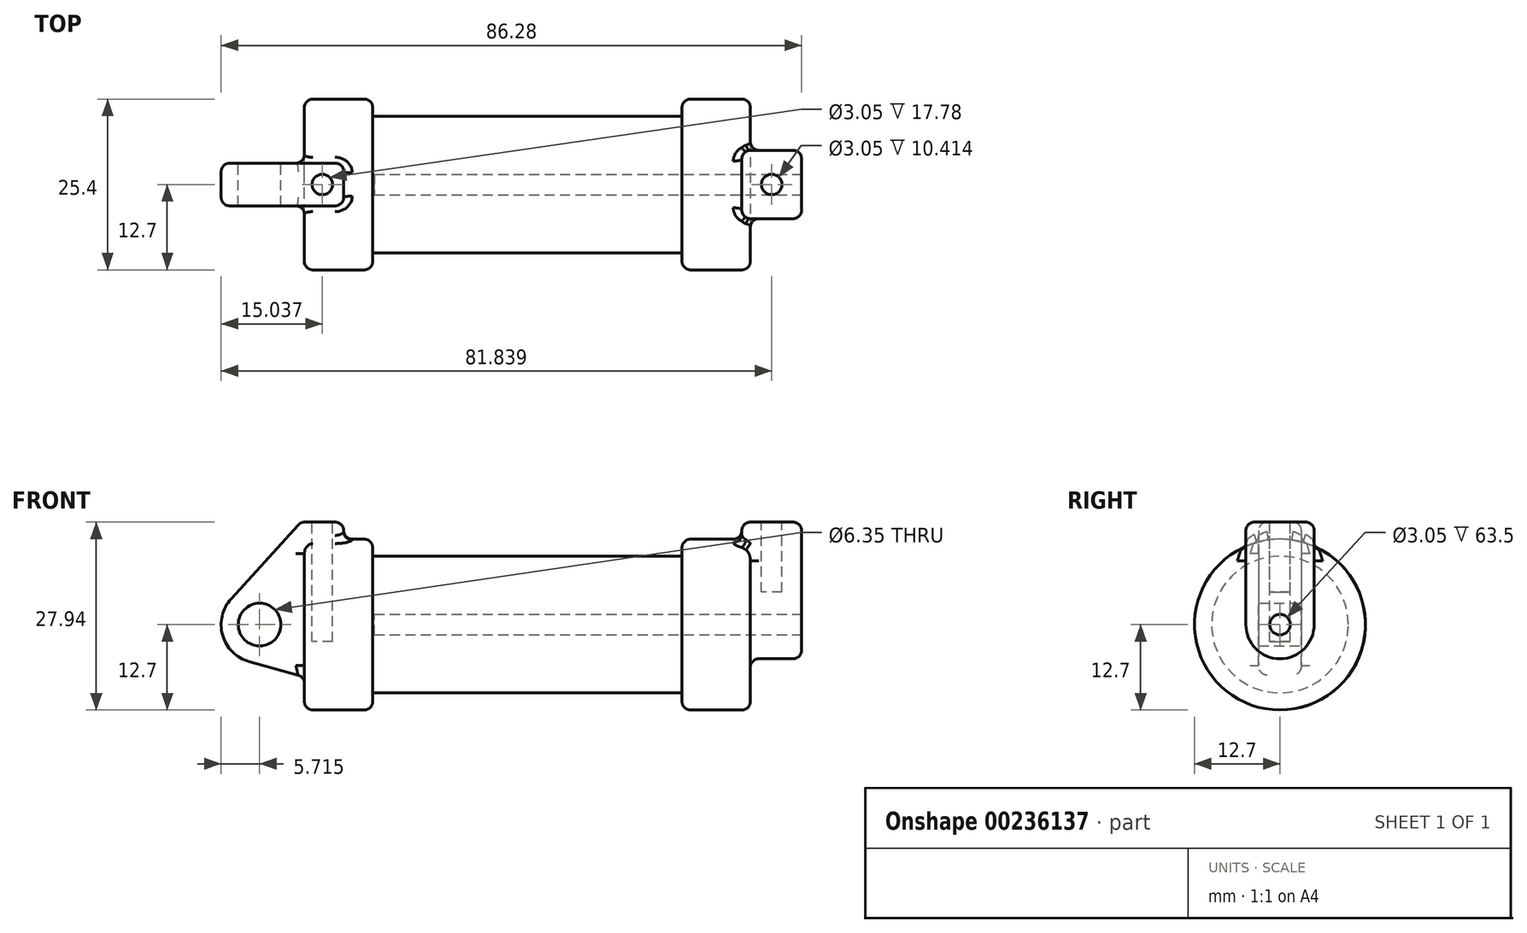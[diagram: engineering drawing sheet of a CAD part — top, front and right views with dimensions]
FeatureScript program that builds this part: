
annotation { "Feature Type Name" : "Feature", "Feature Type Description" : "" }
export const myFeature = defineFeature(function(context is Context, id is Id, definition is map)
    precondition{}
    {
        {
            var Q0;
            Q0=qCreatedBy(makeId("Front.planeOp"),FACE);
            var sketch = newSketch(context, id + "F0", { "sketchPlane" : qUnion([Q0])});
            skLineSegment(sketch, "E0", {"start": v(0, 0) * mm, "end": v(0, 12.7) * mm});
            skLineSegment(sketch, "E1", {"start": v(0, 12.7) * mm, "end": v(10.16, 12.7) * mm});
            skLineSegment(sketch, "E2", {"start": v(10.16, 12.7) * mm, "end": v(10.16, 10.16) * mm});
            skLineSegment(sketch, "E3", {"start": v(10.16, 10.16) * mm, "end": v(56.13, 10.16) * mm});
            skLineSegment(sketch, "E4", {"start": v(56.13, 10.16) * mm, "end": v(56.13, 12.7) * mm});
            skLineSegment(sketch, "E5", {"start": v(56.13, 12.7) * mm, "end": v(66.3, 12.7) * mm});
            skLineSegment(sketch, "E6", {"start": v(66.3, 12.7) * mm, "end": v(66.3, 0) * mm});
            skLineSegment(sketch, "E7", {"start": v(66.3, 0) * mm, "end": v(0, 0) * mm});
            skLineSegment(sketch, "E8", {"start": v(5.84, 15.24) * mm, "end": v(-0.5, 15.24) * mm});
            skLineSegment(sketch, "E9", {"start": v(-0.5, 15.24) * mm, "end": v(-10.88, 3.85) * mm});
            skLineSegment(sketch, "E10", {"start": v(0, 0) * mm, "end": v(-6.65, 0) * mm});
            skCircle(sketch, "E11", {"center": v(-6.65, 0) * mm, "radius": 5.72 * mm});
            skCircle(sketch, "E12", {"center": v(-6.65, 0) * mm, "radius": 3.18 * mm});
            skLineSegment(sketch, "E13", {"start": v(5.84, 15.24) * mm, "end": v(5.84, -9.4) * mm});
            skLineSegment(sketch, "E14", {"start": v(5.84, -9.4) * mm, "end": v(-8.18, -5.5) * mm});
            skSolve(sketch);
        }
        {
            var Q0;
            {var subQ0=sQuery(id+"F0.wireOp",EDGE,"E2");Q0=makeQuery(id+"F0.imprint","IMPRINT",FACE,{"disambiguationData":[TD([[makeQuery(id+"F0.imprint","IMPRINT",EDGE,{"derivedFrom":subQ0}),-1.0]])]});}
            var Q1;
            {var subQ0=sQuery(id+"F0.wireOp",EDGE,"E0");Q1=makeQuery(id+"F0.imprint","IMPRINT",FACE,{"disambiguationData":[TD([[makeQuery(id+"F0.imprint","IMPRINT",EDGE,{"derivedFrom":subQ0}),-1.0]])]});}
            var Q2;
            Q2=sQuery(id+"F0.wireOp",EDGE,"E7");
            revolve(context, id + "F1", {"entities" : qUnion([Q0, Q1]), "axis" : qUnion([Q2]), "revolveType" : RevolveType.FULL});
        }
        {
            var Q0;
            {var subQ0=sQuery(id+"F0.wireOp",EDGE,"E0");Q0=makeQuery(id+"F0.imprint","IMPRINT",FACE,{"disambiguationData":[TD([[makeQuery(id+"F0.imprint","IMPRINT",EDGE,{"derivedFrom":subQ0}),-1.0]])]});}
            var Q1;
            {var subQ0=sQuery(id+"F0.wireOp",EDGE,"E14");Q1=makeQuery(id+"F0.imprint","IMPRINT",FACE,{"disambiguationData":[TD([[makeQuery(id+"F0.imprint","IMPRINT",EDGE,{"derivedFrom":subQ0}),-1.0]])]});}
            var Q2;
            {var subQ4=sQuery(id+"F0.wireOp",EDGE,"E12");Q2=makeQuery(id+"F0.imprint","IMPRINT",FACE,{"disambiguationData":[TD([[makeQuery(id+"F0.imprint","IMPRINT",EDGE,{"derivedFrom":subQ4}),-1.0]])]});}
            var Q3;
            {var subQ3=sQuery(id+"F0.wireOp",EDGE,"E0");Q3=makeQuery(id+"F0.imprint","IMPRINT",FACE,{"disambiguationData":[TD([[makeQuery(id+"F0.imprint","IMPRINT",EDGE,{"derivedFrom":subQ3}),1.0]])]});}
            extrude(context, id + "F2", {"entities" : qUnion([Q0, Q1, Q2, Q3]), "operationType" : NewBodyOperationType.ADD, "endBound" : BoundingType.SYMMETRIC, "depth" : 6.35 * mm});
        }
        {
            var Q0;
            Q0=makeQuery(id+"F1.opRevolve","SWEPT_FACE",FACE,{"disambiguationData":[OSD([sQuery(id+"F0.wireOp",EDGE,"E6")])]});
            var sketch = newSketch(context, id + "F3", { "sketchPlane" : qUnion([Q0])});
            skCircle(sketch, "E15", {"center": v(0, 0) * mm, "radius": 5.08 * mm});
            skLineSegment(sketch, "E16", {"start": v(5.08, 0) * mm, "end": v(5.08, 15.24) * mm});
            skLineSegment(sketch, "E17", {"start": v(5.08, 15.24) * mm, "end": v(-5.08, 15.24) * mm});
            skLineSegment(sketch, "E18", {"start": v(-5.08, 15.24) * mm, "end": v(-5.08, 0) * mm});
            skSolve(sketch);
        }
        {
            var Q0;
            Q0 = qSketchRegion(id + "F3", true);
            extrude(context, id + "F4", {"entities" : qUnion([Q0]), "operationType" : NewBodyOperationType.ADD, "depth" : 7.62 * mm, "hasSecondDirection" : true, "secondDirectionOppositeDirection" : true, "secondDirectionDepth" : 1.27 * mm});
        }
        {
            var Q0;
            Q0=makeQuery(id+"F4.opExtrude","CAP_FACE",FACE,{"disambiguationData":[OSD([sQuery(id+"F3.wireOp",EDGE,"E15"),sQuery(id+"F3.wireOp",EDGE,"E16"),sQuery(id+"F3.wireOp",EDGE,"E17"),sQuery(id+"F3.wireOp",EDGE,"E18")])],"isStart":false});
            var sketch = newSketch(context, id + "F5", { "sketchPlane" : qUnion([Q0])});
            skCircle(sketch, "E19", {"center": v(0, 0) * mm, "radius": 1.52 * mm});
            skSolve(sketch);
        }
        {
            var Q0;
            Q0 = qSketchRegion(id + "F5", true);
            extrude(context, id + "F6", {"entities" : qUnion([Q0]), "operationType" : NewBodyOperationType.REMOVE, "oppositeDirection" : true, "depth" : 63.5 * mm});
        }
        {
            var Q0;
            Q0=makeQuery(id+"F2.opExtrude","SWEPT_FACE",FACE,{"disambiguationData":[OSD([sQuery(id+"F0.wireOp",EDGE,"E8")])]});
            var sketch = newSketch(context, id + "F7", { "sketchPlane" : qUnion([Q0])});
            skCircle(sketch, "E20", {"center": v(2.67, 0) * mm, "radius": 1.52 * mm});
            skPoint(sketch, "E20.centerSnap0", {"position": v(5.84, 0) * mm});
            skPoint(sketch, "E20.centerSnap1", {"position": v(2.67, 3.18) * mm});
            skSolve(sketch);
        }
        {
            var Q0;
            {var subQ0=sQuery(id+"F3.wireOp",EDGE,"E17");Q0=makeQuery(id+"FxH4axhwVwaUUZh_1.boolean.opBoolean","MERGE",FACE,{"derivedFrom":[makeQuery(id+"F4.opExtrude","SWEPT_FACE",FACE,{"disambiguationData":[OSD([subQ0])]}),makeQuery(id+"FxH4axhwVwaUUZh_1.opExtrude","SWEPT_FACE",FACE,{"disambiguationData":[OSD([subQ0])]})]});}
            var sketch = newSketch(context, id + "F8", { "sketchPlane" : qUnion([Q0])});
            skCircle(sketch, "E21", {"center": v(69.47, 0) * mm, "radius": 1.52 * mm});
            skPoint(sketch, "E21.centerSnap0", {"position": v(73.91, 0) * mm});
            skPoint(sketch, "E21.centerSnap1", {"position": v(69.47, 5.08) * mm});
            skSolve(sketch);
        }
        {
            var Q0;
            Q0 = qSketchRegion(id + "F7", true);
            extrude(context, id + "F9", {"entities" : qUnion([Q0]), "operationType" : NewBodyOperationType.REMOVE, "oppositeDirection" : true, "depth" : 17.78 * mm});
        }
        {
            var Q0;
            Q0 = qSketchRegion(id + "F8", true);
            extrude(context, id + "F10", {"entities" : qUnion([Q0]), "operationType" : NewBodyOperationType.REMOVE, "oppositeDirection" : true, "depth" : 10.4 * mm});
        }
        {
            var Q0;
            Q0=makeQuery(id+"F1.opRevolve","SWEPT_EDGE",EDGE,{"disambiguationData":[OSD([sQuery(id+"F0.wireOp",EDGE,"E0"),sQuery(id+"F0.wireOp",EDGE,"E1")])]});
            var Q1;
            Q1=makeQuery(id+"F1.opRevolve","SWEPT_EDGE",EDGE,{"disambiguationData":[OSD([sQuery(id+"F0.wireOp",EDGE,"E1"),sQuery(id+"F0.wireOp",EDGE,"E2")])]});
            var Q2;
            Q2=makeQuery(id+"F1.opRevolve","SWEPT_EDGE",EDGE,{"disambiguationData":[OSD([sQuery(id+"F0.wireOp",EDGE,"E4"),sQuery(id+"F0.wireOp",EDGE,"E5")])]});
            var Q3;
            Q3=makeQuery(id+"F4.boolean.opBoolean","SPLIT",EDGE,{"disambiguationData":[OD(1.0)],"derivedFrom":makeQuery(id+"F1.opRevolve","SWEPT_EDGE",EDGE,{"disambiguationData":[OSD([sQuery(id+"F0.wireOp",EDGE,"E5"),sQuery(id+"F0.wireOp",EDGE,"E6")])]})});
            fillet(context, id + "F11", {"entities" : qUnion([Q0, Q1, Q2, Q3]), "radius" : 1.27 * mm, "tangentPropagation" : true, "allowEdgeOverflow" : false});
        }
        {
            var Q0;
            Q0=makeQuery(id+"F2.opExtrude","CAP_EDGE",EDGE,{"disambiguationData":[OSD([sQuery(id+"F0.wireOp",EDGE,"E8")])],"isStart":false});
            var Q1;
            Q1=makeQuery(id+"F2.opExtrude","SWEPT_EDGE",EDGE,{"disambiguationData":[OSD([sQuery(id+"F0.wireOp",EDGE,"E8"),sQuery(id+"F0.wireOp",EDGE,"E13")])]});
            var Q2;
            Q2=makeQuery(id+"F2.opExtrude","CAP_EDGE",EDGE,{"disambiguationData":[OSD([sQuery(id+"F0.wireOp",EDGE,"E8")])],"isStart":true});
            var Q3;
            Q3=makeQuery(id+"F2.opExtrude","SWEPT_EDGE",EDGE,{"disambiguationData":[OSD([sQuery(id+"F0.wireOp",EDGE,"E8"),sQuery(id+"F0.wireOp",EDGE,"E9")])]});
            var Q4;
            Q4=makeQuery(id+"F2.opExtrude","CAP_EDGE",EDGE,{"disambiguationData":[OSD([sQuery(id+"F0.wireOp",EDGE,"E9")])],"isStart":false});
            var Q5;
            Q5=makeQuery(id+"F2.opExtrude","CAP_EDGE",EDGE,{"disambiguationData":[OSD([sQuery(id+"F0.wireOp",EDGE,"E9")])],"isStart":true});
            var Q6;
            Q6=makeQuery(id+"F2.opExtrude","CAP_EDGE",EDGE,{"disambiguationData":[OSD([sQuery(id+"F0.wireOp",EDGE,"E11")])],"isStart":true});
            var Q7;
            Q7=makeQuery(id+"F2.opExtrude","CAP_EDGE",EDGE,{"disambiguationData":[OSD([sQuery(id+"F0.wireOp",EDGE,"E11")])],"isStart":false});
            var Q8;
            Q8=makeQuery(id+"F2.opExtrude","CAP_EDGE",EDGE,{"disambiguationData":[OSD([sQuery(id+"F0.wireOp",EDGE,"E14")])],"isStart":false});
            var Q9;
            Q9=makeQuery(id+"F2.opExtrude","CAP_EDGE",EDGE,{"disambiguationData":[OSD([sQuery(id+"F0.wireOp",EDGE,"E14")])],"isStart":true});
            var Q10;
            Q10=makeQuery(id+"F2.boolean.opBoolean","INTERSECT",EDGE,{"derivedFrom":[makeQuery(id+"F1.opRevolve","SWEPT_FACE",FACE,{"disambiguationData":[OSD([sQuery(id+"F0.wireOp",EDGE,"E1")])]}),makeQuery(id+"F2.opExtrude","CAP_FACE",FACE,{"disambiguationData":[OSD([sQuery(id+"F0.wireOp",EDGE,"E8"),sQuery(id+"F0.wireOp",EDGE,"E9"),sQuery(id+"F0.wireOp",EDGE,"E11"),sQuery(id+"F0.wireOp",EDGE,"E12"),sQuery(id+"F0.wireOp",EDGE,"E13"),sQuery(id+"F0.wireOp",EDGE,"E14")])],"isStart":false})]});
            var Q11;
            Q11=makeQuery(id+"F2.boolean.opBoolean","INTERSECT",EDGE,{"derivedFrom":[makeQuery(id+"F1.opRevolve","SWEPT_FACE",FACE,{"disambiguationData":[OSD([sQuery(id+"F0.wireOp",EDGE,"E1")])]}),makeQuery(id+"F2.opExtrude","SWEPT_FACE",FACE,{"disambiguationData":[OSD([sQuery(id+"F0.wireOp",EDGE,"E13")])]})]});
            var Q12;
            Q12=makeQuery(id+"F2.boolean.opBoolean","INTERSECT",EDGE,{"derivedFrom":[makeQuery(id+"F1.opRevolve","SWEPT_FACE",FACE,{"disambiguationData":[OSD([sQuery(id+"F0.wireOp",EDGE,"E1")])]}),makeQuery(id+"F2.opExtrude","CAP_FACE",FACE,{"disambiguationData":[OSD([sQuery(id+"F0.wireOp",EDGE,"E8"),sQuery(id+"F0.wireOp",EDGE,"E9"),sQuery(id+"F0.wireOp",EDGE,"E11"),sQuery(id+"F0.wireOp",EDGE,"E12"),sQuery(id+"F0.wireOp",EDGE,"E13"),sQuery(id+"F0.wireOp",EDGE,"E14")])],"isStart":true})]});
            var Q13;
            Q13=makeQuery(id+"F2.boolean.opBoolean","INTERSECT",EDGE,{"derivedFrom":[makeQuery(id+"F1.opRevolve","SWEPT_FACE",FACE,{"disambiguationData":[OSD([sQuery(id+"F0.wireOp",EDGE,"E0")])]}),makeQuery(id+"F2.opExtrude","CAP_FACE",FACE,{"disambiguationData":[OSD([sQuery(id+"F0.wireOp",EDGE,"E8"),sQuery(id+"F0.wireOp",EDGE,"E9"),sQuery(id+"F0.wireOp",EDGE,"E11"),sQuery(id+"F0.wireOp",EDGE,"E12"),sQuery(id+"F0.wireOp",EDGE,"E13"),sQuery(id+"F0.wireOp",EDGE,"E14")])],"isStart":true})]});
            var Q14;
            Q14=makeQuery(id+"F11.opFillet","BLEND_EDGE",EDGE,{"blendedFrom":[makeQuery(id+"F1.opRevolve","SWEPT_EDGE",EDGE,{"disambiguationData":[OSD([sQuery(id+"F0.wireOp",EDGE,"E0"),sQuery(id+"F0.wireOp",EDGE,"E1")])]}),makeQuery(id+"F2.opExtrude","CAP_FACE",FACE,{"disambiguationData":[OSD([sQuery(id+"F0.wireOp",EDGE,"E8"),sQuery(id+"F0.wireOp",EDGE,"E9"),sQuery(id+"F0.wireOp",EDGE,"E11"),sQuery(id+"F0.wireOp",EDGE,"E12"),sQuery(id+"F0.wireOp",EDGE,"E13"),sQuery(id+"F0.wireOp",EDGE,"E14")])],"isStart":true})],"blendedInto":[makeQuery(id+"F2.opExtrude","CAP_FACE",FACE,{"disambiguationData":[OSD([sQuery(id+"F0.wireOp",EDGE,"E8"),sQuery(id+"F0.wireOp",EDGE,"E9"),sQuery(id+"F0.wireOp",EDGE,"E11"),sQuery(id+"F0.wireOp",EDGE,"E12"),sQuery(id+"F0.wireOp",EDGE,"E13"),sQuery(id+"F0.wireOp",EDGE,"E14")])],"isStart":true})]});
            var Q15;
            Q15=makeQuery(id+"F2.boolean.opBoolean","INTERSECT",EDGE,{"derivedFrom":[makeQuery(id+"F1.opRevolve","SWEPT_FACE",FACE,{"disambiguationData":[OSD([sQuery(id+"F0.wireOp",EDGE,"E0")])]}),makeQuery(id+"F2.opExtrude","SWEPT_FACE",FACE,{"disambiguationData":[OSD([sQuery(id+"F0.wireOp",EDGE,"E14")])]})]});
            var Q16;
            Q16=makeQuery(id+"F2.boolean.opBoolean","INTERSECT",EDGE,{"derivedFrom":[makeQuery(id+"F1.opRevolve","SWEPT_FACE",FACE,{"disambiguationData":[OSD([sQuery(id+"F0.wireOp",EDGE,"E0")])]}),makeQuery(id+"F2.opExtrude","CAP_FACE",FACE,{"disambiguationData":[OSD([sQuery(id+"F0.wireOp",EDGE,"E8"),sQuery(id+"F0.wireOp",EDGE,"E9"),sQuery(id+"F0.wireOp",EDGE,"E11"),sQuery(id+"F0.wireOp",EDGE,"E12"),sQuery(id+"F0.wireOp",EDGE,"E13"),sQuery(id+"F0.wireOp",EDGE,"E14")])],"isStart":false})]});
            var Q17;
            Q17=makeQuery(id+"F11.opFillet","BLEND_EDGE",EDGE,{"blendedFrom":[makeQuery(id+"F1.opRevolve","SWEPT_EDGE",EDGE,{"disambiguationData":[OSD([sQuery(id+"F0.wireOp",EDGE,"E0"),sQuery(id+"F0.wireOp",EDGE,"E1")])]}),makeQuery(id+"F2.opExtrude","CAP_FACE",FACE,{"disambiguationData":[OSD([sQuery(id+"F0.wireOp",EDGE,"E8"),sQuery(id+"F0.wireOp",EDGE,"E9"),sQuery(id+"F0.wireOp",EDGE,"E11"),sQuery(id+"F0.wireOp",EDGE,"E12"),sQuery(id+"F0.wireOp",EDGE,"E13"),sQuery(id+"F0.wireOp",EDGE,"E14")])],"isStart":false})],"blendedInto":[makeQuery(id+"F2.opExtrude","CAP_FACE",FACE,{"disambiguationData":[OSD([sQuery(id+"F0.wireOp",EDGE,"E8"),sQuery(id+"F0.wireOp",EDGE,"E9"),sQuery(id+"F0.wireOp",EDGE,"E11"),sQuery(id+"F0.wireOp",EDGE,"E12"),sQuery(id+"F0.wireOp",EDGE,"E13"),sQuery(id+"F0.wireOp",EDGE,"E14")])],"isStart":false})]});
            var Q18;
            Q18=makeQuery(id+"F2.opExtrude","CAP_EDGE",EDGE,{"disambiguationData":[OSD([sQuery(id+"F0.wireOp",EDGE,"E13")])],"isStart":false});
            var Q19;
            Q19=makeQuery(id+"F2.opExtrude","CAP_EDGE",EDGE,{"disambiguationData":[OSD([sQuery(id+"F0.wireOp",EDGE,"E13")])],"isStart":true});
            fillet(context, id + "F12", {"entities" : qUnion([Q0, Q1, Q2, Q3, Q4, Q5, Q6, Q7, Q8, Q9, Q10, Q11, Q12, Q13, Q14, Q15, Q16, Q17, Q18, Q19]), "radius" : 1.27 * mm, "tangentPropagation" : true, "allowEdgeOverflow" : false});
        }
        {
            var Q0;
            Q0=makeQuery(id+"F4.opExtrude","CAP_EDGE",EDGE,{"disambiguationData":[OSD([sQuery(id+"F3.wireOp",EDGE,"E18")])],"isStart":false});
            var Q1;
            Q1=makeQuery(id+"F4.opExtrude","CAP_EDGE",EDGE,{"disambiguationData":[OSD([sQuery(id+"F3.wireOp",EDGE,"E17")])],"isStart":false});
            var Q2;
            Q2=makeQuery(id+"F4.opExtrude","SWEPT_EDGE",EDGE,{"disambiguationData":[OSD([sQuery(id+"F3.wireOp",EDGE,"E17"),sQuery(id+"F3.wireOp",EDGE,"E18")])]});
            var Q3;
            Q3=makeQuery(id+"F4.opExtrude","SWEPT_EDGE",EDGE,{"disambiguationData":[OSD([sQuery(id+"F3.wireOp",EDGE,"E16"),sQuery(id+"F3.wireOp",EDGE,"E17")])]});
            var Q4;
            Q4=makeQuery(id+"F4.opExtrude","CAP_EDGE",EDGE,{"disambiguationData":[OSD([sQuery(id+"F3.wireOp",EDGE,"E17")])],"isStart":true});
            var Q5;
            Q5=makeQuery(id+"F11.opFillet","BLEND_EDGE",EDGE,{"blendedFrom":[makeQuery(id+"F1.opRevolve","SWEPT_EDGE",EDGE,{"disambiguationData":[OSD([sQuery(id+"F0.wireOp",EDGE,"E5"),sQuery(id+"F0.wireOp",EDGE,"E6")])]}),makeQuery(id+"F4.opExtrude","SWEPT_FACE",FACE,{"disambiguationData":[OSD([sQuery(id+"F3.wireOp",EDGE,"E18")])]})],"blendedInto":[makeQuery(id+"F4.opExtrude","SWEPT_FACE",FACE,{"disambiguationData":[OSD([sQuery(id+"F3.wireOp",EDGE,"E18")])]})]});
            var Q6;
            Q6=makeQuery(id+"F4.opExtrude","CAP_EDGE",EDGE,{"disambiguationData":[OSD([sQuery(id+"F3.wireOp",EDGE,"E18")])],"isStart":true});
            var Q7;
            Q7=makeQuery(id+"F4.boolean.opBoolean","INTERSECT",EDGE,{"derivedFrom":[makeQuery(id+"F1.opRevolve","SWEPT_FACE",FACE,{"disambiguationData":[OSD([sQuery(id+"F0.wireOp",EDGE,"E6")])]}),makeQuery(id+"F4.opExtrude","SWEPT_FACE",FACE,{"disambiguationData":[OSD([sQuery(id+"F3.wireOp",EDGE,"E18")])]})]});
            var Q8;
            Q8=makeQuery(id+"F4.boolean.opBoolean","INTERSECT",EDGE,{"derivedFrom":[makeQuery(id+"F1.opRevolve","SWEPT_FACE",FACE,{"disambiguationData":[OSD([sQuery(id+"F0.wireOp",EDGE,"E6")])]}),makeQuery(id+"F4.opExtrude","SWEPT_FACE",FACE,{"disambiguationData":[OSD([sQuery(id+"F3.wireOp",EDGE,"E15")])]})]});
            var Q9;
            Q9=makeQuery(id+"F4.opExtrude","CAP_EDGE",EDGE,{"disambiguationData":[OSD([sQuery(id+"F3.wireOp",EDGE,"E15")])],"isStart":false});
            var Q10;
            Q10=makeQuery(id+"F4.opExtrude","CAP_EDGE",EDGE,{"disambiguationData":[OSD([sQuery(id+"F3.wireOp",EDGE,"E16")])],"isStart":false});
            var Q11;
            Q11=makeQuery(id+"F4.boolean.opBoolean","INTERSECT",EDGE,{"derivedFrom":[makeQuery(id+"F1.opRevolve","SWEPT_FACE",FACE,{"disambiguationData":[OSD([sQuery(id+"F0.wireOp",EDGE,"E6")])]}),makeQuery(id+"F4.opExtrude","SWEPT_FACE",FACE,{"disambiguationData":[OSD([sQuery(id+"F3.wireOp",EDGE,"E16")])]})]});
            var Q12;
            Q12=makeQuery(id+"F11.opFillet","BLEND_EDGE",EDGE,{"blendedFrom":[makeQuery(id+"F1.opRevolve","SWEPT_EDGE",EDGE,{"disambiguationData":[OSD([sQuery(id+"F0.wireOp",EDGE,"E5"),sQuery(id+"F0.wireOp",EDGE,"E6")])]}),makeQuery(id+"F4.opExtrude","SWEPT_FACE",FACE,{"disambiguationData":[OSD([sQuery(id+"F3.wireOp",EDGE,"E16")])]})],"blendedInto":[makeQuery(id+"F4.opExtrude","SWEPT_FACE",FACE,{"disambiguationData":[OSD([sQuery(id+"F3.wireOp",EDGE,"E16")])]})]});
            var Q13;
            Q13=makeQuery(id+"F4.opExtrude","CAP_EDGE",EDGE,{"disambiguationData":[OSD([sQuery(id+"F3.wireOp",EDGE,"E16")])],"isStart":true});
            var Q14;
            Q14=makeQuery(id+"F4.boolean.opBoolean","INTERSECT",EDGE,{"derivedFrom":[makeQuery(id+"F1.opRevolve","SWEPT_FACE",FACE,{"disambiguationData":[OSD([sQuery(id+"F0.wireOp",EDGE,"E5")])]}),makeQuery(id+"F4.opExtrude","CAP_FACE",FACE,{"disambiguationData":[OSD([sQuery(id+"F3.wireOp",EDGE,"E15"),sQuery(id+"F3.wireOp",EDGE,"E16"),sQuery(id+"F3.wireOp",EDGE,"E17"),sQuery(id+"F3.wireOp",EDGE,"E18")])],"isStart":true})]});
            fillet(context, id + "F13", {"entities" : qUnion([Q0, Q1, Q2, Q3, Q4, Q5, Q6, Q7, Q8, Q9, Q10, Q11, Q12, Q13, Q14]), "radius" : 1.27 * mm, "tangentPropagation" : true, "allowEdgeOverflow" : false});
        }
    });
